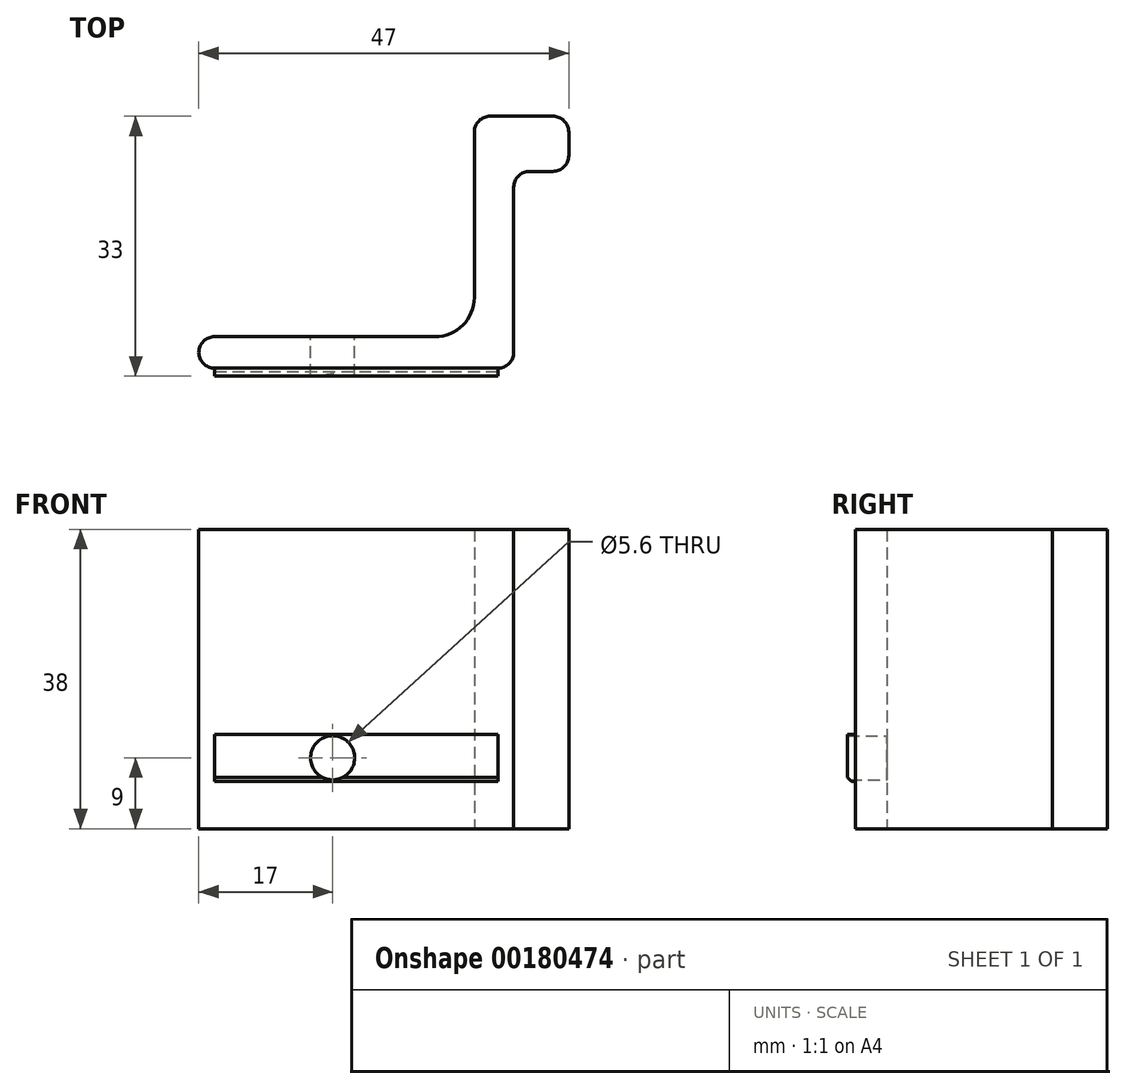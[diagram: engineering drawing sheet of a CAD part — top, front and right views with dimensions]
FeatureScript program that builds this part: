
annotation { "Feature Type Name" : "Feature", "Feature Type Description" : "" }
export const myFeature = defineFeature(function(context is Context, id is Id, definition is map)
    precondition{}
    {
        {
            var Q0;
            Q0=qCreatedBy(makeId("Top.planeOp"),FACE);
            var sketch = newSketch(context, id + "F0", { "sketchPlane" : qUnion([Q0])});
            skLineSegment(sketch, "E0.bottom", {"start": v(2, 0) * mm, "end": v(38, 0) * mm});
            skLineSegment(sketch, "E0.top", {"start": v(37, 32) * mm, "end": v(40, 32) * mm});
            skLineSegment(sketch, "E0.left", {"start": v(0, 2) * mm, "end": v(0, 2) * mm});
            skLineSegment(sketch, "E0.right", {"start": v(40, 2) * mm, "end": v(40, 23) * mm});
            skLineSegment(sketch, "E1.bottom", {"start": v(40, 32) * mm, "end": v(45, 32) * mm});
            skLineSegment(sketch, "E1.top", {"start": v(42, 25) * mm, "end": v(45, 25) * mm});
            skLineSegment(sketch, "E1.right", {"start": v(47, 30) * mm, "end": v(47, 27) * mm});
            skLineSegment(sketch, "E2.top", {"start": v(2, 4) * mm, "end": v(30, 4) * mm});
            skLineSegment(sketch, "E2.right", {"start": v(35, 30) * mm, "end": v(35, 9) * mm});
            skPoint(sketch, "E3.visualSharp", {"position": v(35, 4) * mm});
            skArc(sketch, "E3.filletArc", {"start": v(30, 4) * mm, "mid": v(33.54, 5.46) * mm, "end": v(35, 9) * mm});
            skPoint(sketch, "E4.visualSharp", {"position": v(47, 32) * mm});
            skArc(sketch, "E4.filletArc", {"start": v(47, 30) * mm, "mid": v(46.41, 31.41) * mm, "end": v(45, 32) * mm});
            skPoint(sketch, "E5.visualSharp", {"position": v(47, 25) * mm});
            skArc(sketch, "E5.filletArc", {"start": v(45, 25) * mm, "mid": v(46.41, 25.59) * mm, "end": v(47, 27) * mm});
            skPoint(sketch, "E6.visualSharp", {"position": v(35, 32) * mm});
            skArc(sketch, "E6.filletArc", {"start": v(37, 32) * mm, "mid": v(35.59, 31.41) * mm, "end": v(35, 30) * mm});
            skPoint(sketch, "E7.visualSharp", {"position": v(40, 0) * mm});
            skArc(sketch, "E7.filletArc", {"start": v(38, 0) * mm, "mid": v(39.41, 0.59) * mm, "end": v(40, 2) * mm});
            skPoint(sketch, "E8.visualSharp", {"position": v(0, 4) * mm});
            skArc(sketch, "E8.filletArc", {"start": v(2, 4) * mm, "mid": v(0.59, 3.41) * mm, "end": v(0, 2) * mm});
            skPoint(sketch, "E9.visualSharp", {"position": v(40, 25) * mm});
            skArc(sketch, "E9.filletArc", {"start": v(42, 25) * mm, "mid": v(40.59, 24.41) * mm, "end": v(40, 23) * mm});
            skPoint(sketch, "E10.visualSharp", {"position": v(0, 0) * mm});
            skArc(sketch, "E10.filletArc", {"start": v(0, 2) * mm, "mid": v(0.59, 0.59) * mm, "end": v(2, 0) * mm});
            skSolve(sketch);
        }
        {
            var Q0;
            Q0=makeQuery(id+"F0.imprint","IMPRINT",FACE,{"disambiguationData":[TD([[makeQuery(id+"F0.imprint","IMPRINT",EDGE,{"derivedFrom":sQuery(id+"F0.wireOp",EDGE,"E0.bottom")}),1.0]])]});
            extrude(context, id + "F1", {"entities" : qUnion([Q0]), "depth" : 38 * mm});
        }
        {
            var Q0;
            Q0=makeQuery(id+"F1.opExtrude","SWEPT_FACE",FACE,{"disambiguationData":[OSD([sQuery(id+"F0.wireOp",EDGE,"E0.bottom")])]});
            var sketch = newSketch(context, id + "F2", { "sketchPlane" : qUnion([Q0])});
            skLineSegment(sketch, "E11.bottom", {"start": v(2, 0) * mm, "end": v(38, 0) * mm});
            skLineSegment(sketch, "E11.top", {"start": v(2, 6) * mm, "end": v(38, 6) * mm});
            skLineSegment(sketch, "E11.left", {"start": v(2, 0) * mm, "end": v(2, 6) * mm});
            skLineSegment(sketch, "E11.right", {"start": v(38, 0) * mm, "end": v(38, 6) * mm});
            skLineSegment(sketch, "E12.top", {"start": v(2, 12) * mm, "end": v(38, 12) * mm});
            skLineSegment(sketch, "E12.left", {"start": v(2, 6) * mm, "end": v(2, 12) * mm});
            skLineSegment(sketch, "E12.right", {"start": v(38, 6) * mm, "end": v(38, 12) * mm});
            skCircle(sketch, "E13", {"center": v(17, 9) * mm, "radius": 2.8 * mm});
            skPoint(sketch, "E13.centerSnap0", {"position": v(2, 9) * mm});
            skSolve(sketch);
        }
        {
            var Q0;
            Q0=makeQuery(id+"F2.imprint","IMPRINT",FACE,{"disambiguationData":[TD([[makeQuery(id+"F2.imprint","IMPRINT",EDGE,{"derivedFrom":sQuery(id+"F2.wireOp",EDGE,"E11.top")}),1.0]])]});
            extrude(context, id + "F3", {"entities" : qUnion([Q0]), "operationType" : NewBodyOperationType.ADD, "depth" : 1 * mm});
        }
        {
            var Q0;
            Q0=makeQuery(id+"F3.boolean.opBoolean","SPLIT",FACE,{"disambiguationData":[TD([makeQuery(id+"F3.opExtrude","SWEPT_FACE",FACE,{"disambiguationData":[OSD([sQuery(id+"F2.wireOp",EDGE,"E13")])]})])],"derivedFrom":makeQuery(id+"F1.opExtrude","SWEPT_FACE",FACE,{"disambiguationData":[OSD([sQuery(id+"F0.wireOp",EDGE,"E0.bottom")])]})});
            extrude(context, id + "F4", {"entities" : qUnion([Q0]), "operationType" : NewBodyOperationType.REMOVE, "oppositeDirection" : true, "depth" : 4 * mm});
        }
        {
            var Q0;
            Q0=makeQuery(id+"F3.opExtrude","CAP_EDGE",EDGE,{"disambiguationData":[OSD([sQuery(id+"F2.wireOp",EDGE,"E11.top")])],"isStart":false});
            chamfer(context, id + "F5", {"entities" : qUnion([Q0]), "width" : .5 * mm, "tangentPropagation" : true});
        }
    });
